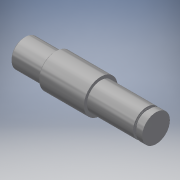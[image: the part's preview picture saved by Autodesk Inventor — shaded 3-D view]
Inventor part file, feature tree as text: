
AUTODESK INVENTOR PART (.ipt)
format: ipt  version: 2019 (Build 230136000, 136)  size: 144,384 bytes
history: native  units: mm
features: other x6, chamfer x2
ambient origin geometry x6: Origin, XZ Plane, XY Plane, X Axis, Y Axis, Z Axis
bodies: Body1 (feature_tree)
feature tree (8):
  other  "實體1"
  other  "迴轉1"
  other  "扣環槽3"
  chamfer  "倒角2"  [1 undecoded]
  chamfer  "倒角1"  Distance=9.0mm
  other  "起始平面"
  other  "主要草圖"
  other  "iFeature27:3"
note: 1 required parameter value undecoded (feature->parameter linkage not recoverable at this tier; creation-order binding heuristic only, values carry confidence <= 0.55)
